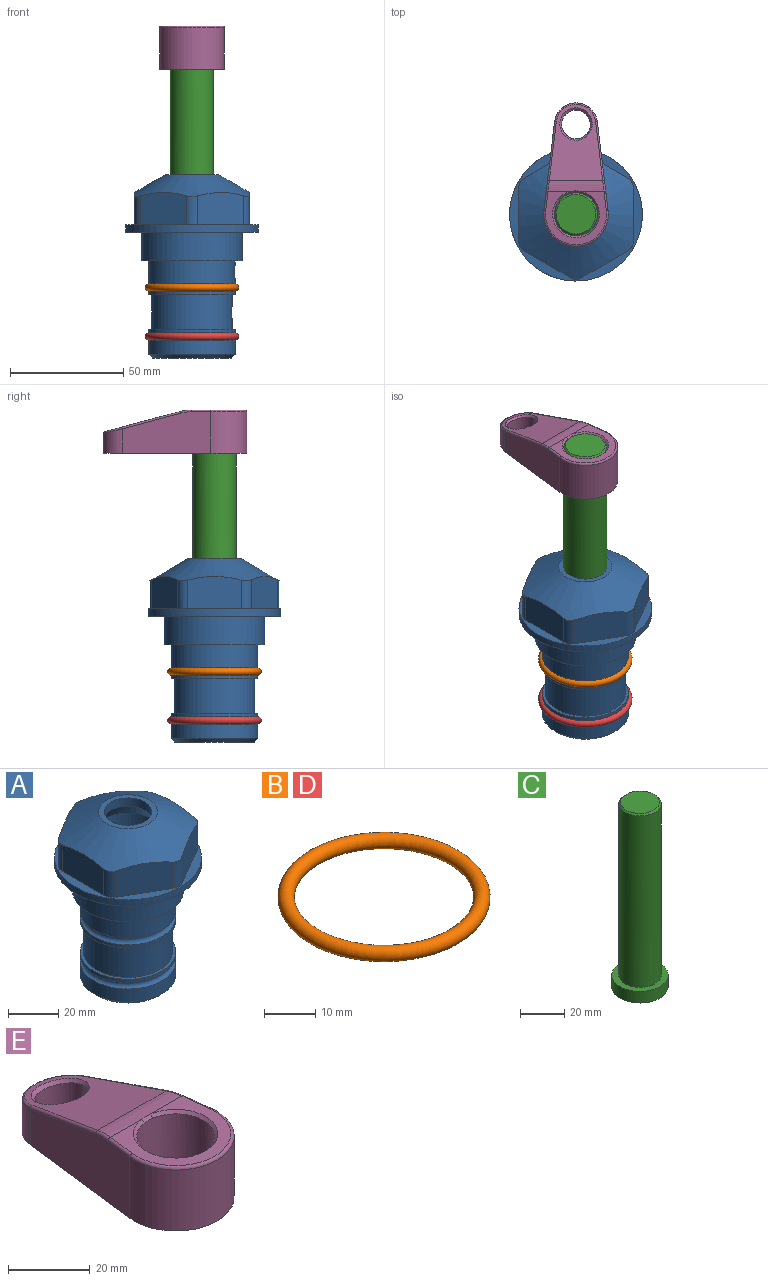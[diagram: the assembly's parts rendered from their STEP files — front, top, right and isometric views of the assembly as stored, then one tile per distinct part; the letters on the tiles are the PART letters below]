
ASSEMBLY  parts=5 mates=4
PART A: 36 faces, bbox 58.7x58.7x81 mm
  f0: cylinder r=17.78mm len=35.56mm, axis (0,0,1), area 1670.8mm2, adj f23,f24,f31
  f1: cylinder r=19.05mm len=38.1mm, axis (0,0,1), area 1191.9mm2, adj f26,f27,f30
  f2: plane 58.66x58.66mm, normal (0,0,-1), area 1150.6mm2, adj f3,f28
  f3: cylinder r=29.33mm len=58.66mm, axis (0,0,-1), area 585.1mm2, adj f2,f4
  f4: plane 58.66x58.66mm, normal (0,0,1), area 475.9mm2, adj f3,f5,f6,f7,f8,f9,f10,f11
  f5: plane 20.32x14.34mm, normal (-0.5,0.87,0), area 324.4mm2, adj f4,f15,f16,f17
  f6: plane 20.32x14.34mm, normal (0.5,0.87,0), area 324.4mm2, adj f4,f14,f15,f17
  f7: plane 23.48x14.34mm, normal (1,0,0), area 324.4mm2, adj f4,f13,f14,f17
  f8: plane 20.32x14.34mm, normal (0.5,-0.87,0), area 324.4mm2, adj f4,f12,f13,f17
  f9: plane 20.32x14.34mm, normal (-0.5,-0.87,0), area 324.4mm2, adj f4,f11,f12,f17
  f10: plane 23.48x14.34mm, normal (-1,0,0), area 324.4mm2, adj f4,f11,f16,f17
  f11: cylinder r=5.08mm len=12.85mm, axis (0,0,-1), area 67.2mm2, adj f4,f9,f10,f17
  f12: cylinder r=5.08mm len=12.85mm, axis (0,0,-1), area 67.2mm2, adj f4,f8,f9,f17
  f13: cylinder r=5.08mm len=12.85mm, axis (0,0,-1), area 67.2mm2, adj f4,f7,f8,f17
  f14: cylinder r=5.08mm len=12.85mm, axis (0,0,-1), area 67.2mm2, adj f4,f6,f7,f17
  f15: cylinder r=5.08mm len=12.85mm, axis (0,0,-1), area 67.2mm2, adj f4,f5,f6,f17
  f16: cylinder r=5.08mm len=12.85mm, axis (0,0,-1), area 67.2mm2, adj f4,f5,f10,f17
  f17: cone r=11.73mm half-angle=60deg, axis (0,0,-1), area 2071.8mm2, adj f5,f6,f7,f8,f9,f10,f11,f12
  f18: plane 23.46x23.46mm, normal (0,0,1), area 147.4mm2, adj f17,f35
  f19: plane 34.93x34.93mm, normal (0,0,-1), area 958mm2, adj f29
  f20: cylinder r=19.05mm len=38.1mm, axis (0,0,1), area 760.1mm2, adj f21,f29
  f21: torus R=19.05mm, axis (0,0,1), area 565.3mm2, adj f20,f22
  f22: cylinder r=19.05mm len=38.1mm, axis (0,0,1), area 190mm2, adj f21,f23
  f23: plane 38.1x38.1mm, normal (0,0,1), area 146.9mm2, adj f0,f22
  f24: plane 38.1x38.1mm, normal (0,0,-1), area 146.9mm2, adj f0,f25
  f25: cylinder r=19.05mm len=38.1mm, axis (0,0,1), area 190mm2, adj f24,f26
  f26: torus R=19.05mm, axis (0,0,1), area 565.3mm2, adj f1,f25
  f27: plane 44.45x44.45mm, normal (0,0,-1), area 411.7mm2, adj f1,f28
  f28: cylinder r=22.23mm len=44.45mm, axis (0,0,1), area 1773.5mm2, adj f2,f27
  f29: cone r=19.05mm half-angle=45deg, axis (0,0,1), area 257.5mm2, adj f19,f20
  f30: cylinder r=3.17mm len=6.75mm, axis (-1,0,0), area 128mm2, adj f1,f33
  f31: cylinder r=3.17mm len=6.35mm, axis (-1,0,0), area 102.5mm2, adj f0,f33
  f32: plane 25.4x25.4mm, normal (0,0,1), area 506.7mm2, adj f33
  f33: cylinder r=12.7mm len=66.42mm, axis (0,0,-1), area 5236.2mm2, adj f30,f31,f32,f34
  f34: cone r=9.53mm half-angle=30deg, axis (0,0,-1), area 443.4mm2, adj f33,f35
  f35: cylinder r=9.53mm len=19.05mm, axis (0,0,-1), area 240.9mm2, adj f18,f34
PART B: 1 faces, bbox 44.7x44.7x3.2 mm
  f0: torus R=19.05mm, axis (0,0,1), area 1193.9mm2
PART C: 6 faces, bbox 25.4x25.4x101.6 mm
  f0: plane 17.46x17.46mm, normal (0,0,1), area 239.5mm2, adj f5
  f1: plane 25.4x25.4mm, normal (0,0,-1), area 506.7mm2, adj f2
  f2: cylinder r=12.7mm len=25.4mm, axis (0,0,1), area 506.7mm2, adj f1,f3
  f3: plane 25.4x25.4mm, normal (0,0,1), area 221.7mm2, adj f2,f4
  f4: cylinder r=9.53mm len=94.46mm, axis (0,0,1), area 5653mm2, adj f3,f5
  f5: cone r=8.73mm half-angle=45deg, axis (0,0,-1), area 64.4mm2, adj f0,f4
PART D: same geometry as B
PART E: 31 faces, bbox 31.7x65.5x19.8 mm
  f0: plane 39.12x18.26mm, normal (0.99,0.12,0), area 612.2mm2, adj f1,f4,f7,f11,f13,f15
  f1: cylinder r=9.53mm len=18.91mm, axis (0,0,-1), area 296.1mm2, adj f0,f2,f7,f17
  f2: plane 39.12x18.26mm, normal (-0.99,0.12,0), area 612.2mm2, adj f1,f4,f7,f12,f14,f16
  f3: cylinder r=6.35mm len=12.7mm, axis (0,0,-1), area 362.4mm2, adj f7,f18
  f4: cylinder r=14.29mm len=28.58mm, axis (0,0,-1), area 882.2mm2, adj f0,f2,f7,f10
  f5: cylinder r=9.53mm len=19.05mm, axis (0,0,-1), area 1092.6mm2, adj f7,f19,f20
  f6: plane 26.99x23.69mm, normal (0,0,1), area 216.2mm2, adj f9,f10,f11,f12,f19
  f7: plane 63.5x28.58mm, normal (0,0,-1), area 661.8mm2, adj f0,f1,f2,f3,f4,f5,f22,f23
  f8: plane 33.52x23.6mm, normal (0,0.26,0.97), area 486mm2, adj f9,f15,f16,f17,f18
  f9: cylinder r=19.05mm len=24.72mm, axis (1,0,0), area 120.4mm2, adj f6,f8,f13,f14,f20
  f10: torus R=13.49mm, axis (0,0,1), area 59mm2, adj f4,f6,f11,f12
  f11: cylinder r=0.79mm len=8.67mm, axis (0.12,-0.99,0), area 10.8mm2, adj f0,f6,f10,f13
  f12: cylinder r=0.79mm len=8.67mm, axis (0.12,0.99,0), area 10.8mm2, adj f2,f6,f10,f14
  f13: bspline ~4.95x1.42mm, area 6.1mm2, adj f0,f9,f11,f15
  f14: bspline ~4.95x1.42mm, area 6.1mm2, adj f2,f9,f12,f16
  f15: cylinder r=0.79mm len=25.95mm, axis (0.12,-0.96,0.26), area 32.9mm2, adj f0,f8,f13,f17
  f16: cylinder r=0.79mm len=25.95mm, axis (0.12,0.96,-0.26), area 32.9mm2, adj f2,f8,f14,f17
  f17: bspline ~18.91x8.38mm, area 30mm2, adj f1,f8,f15,f16
  f18: bspline ~14.29x14.29mm, area 48.3mm2, adj f3,f8
  f19: cone r=9.53mm half-angle=45deg, axis (0,0,1), area 66.5mm2, adj f5,f6,f20
  f20: bspline ~3.22x0.96mm, area 3.5mm2, adj f5,f9,f19
  f21: plane 2.75x2.72mm, normal (0,0,-1), area 2.9mm2, adj f23,f25,f28
  f22: plane 23.05x15.88mm, normal (-0.99,-0.12,0), area 323.6mm2, adj f7,f25,f26,f27,f28,f29
  f23: plane 23.05x15.88mm, normal (0.99,-0.12,0), area 323.6mm2, adj f7,f21,f25,f27,f28,f30
  f24: cylinder r=9.53mm len=10.69mm, axis (0,0,-1), area 114.7mm2, adj f7,f27,f29,f30
  f25: cylinder r=12.7mm len=20.59mm, axis (0,0,-1), area 381.1mm2, adj f7,f21,f22,f23,f26,f28
  f26: plane 2.75x2.72mm, normal (0,0,-1), area 2.9mm2, adj f22,f25,f28
  f27: plane 19.72x18.37mm, normal (0,-0.26,-0.97), area 291.8mm2, adj f22,f23,f24,f28,f29,f30
  f28: cylinder r=15.88mm len=19.92mm, axis (1,0,0), area 54.8mm2, adj f21,f22,f23,f25,f26,f27
  f29: cylinder r=1.59mm len=11mm, axis (0,0,-1), area 34.7mm2, adj f7,f22,f24,f27
  f30: cylinder r=1.59mm len=11mm, axis (0,0,-1), area 34.7mm2, adj f7,f23,f24,f27
PLACE A at identity fixed
PLACE B at identity
PLACE C t=(0,0,27.55)mm
PLACE D t=(0,0,-21.59)mm
PLACE E t=(0,0,27.55)mm
MATE cylindrical C.f2 <-> A.f0  axis (0,0,-1) through (0,0,-10.55)mm
MATE fastened A.f0 <-> B.f0  axis (0,0,1) through (0,0,-24.51)mm
MATE fastened A.f0 <-> D.f0  axis (0,0,1) through (0,0,-46.1)mm
MATE fastened C.f2 <-> E.f4  axis (0,0,1) through (0,0,90.26)mm
